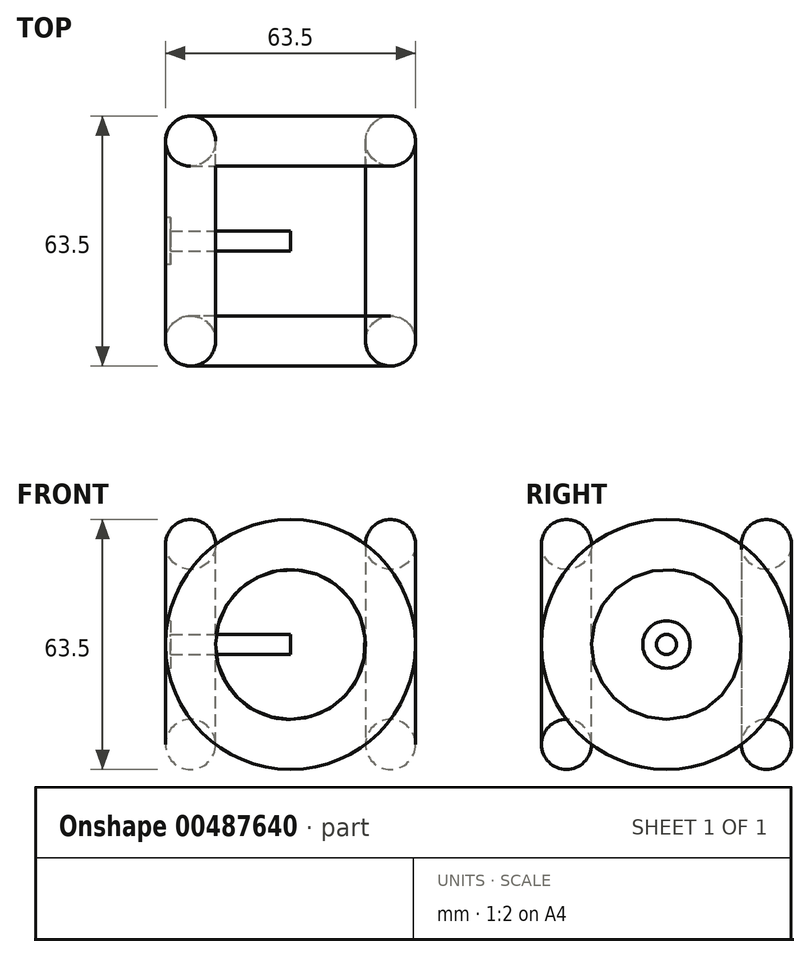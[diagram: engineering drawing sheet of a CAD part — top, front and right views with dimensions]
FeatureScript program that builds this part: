
annotation { "Feature Type Name" : "Feature", "Feature Type Description" : "" }
export const myFeature = defineFeature(function(context is Context, id is Id, definition is map)
    precondition{}
    {
        {
            var Q0;
            Q0=qCreatedBy(makeId("Front.planeOp"),FACE);
            var sketch = newSketch(context, id + "F0", { "sketchPlane" : qUnion([Q0])});
            skLineSegment(sketch, "E0", {"start": v(25.4, 0) * mm, "end": v(25.4, 25.4) * mm});
            skLineSegment(sketch, "E1", {"start": v(25.4, 25.4) * mm, "end": v(-25.4, 25.4) * mm, "construction": true});
            skLineSegment(sketch, "E2", {"start": v(-25.4, 25.4) * mm, "end": v(-25.4, -25.4) * mm, "construction": true});
            skLineSegment(sketch, "E3", {"start": v(-25.4, -25.4) * mm, "end": v(25.4, -25.4) * mm, "construction": true});
            skLineSegment(sketch, "E4", {"start": v(25.4, -25.4) * mm, "end": v(25.4, 0) * mm, "construction": true});
            skLineSegment(sketch, "E5", {"start": v(25.4, 25.4) * mm, "end": v(-25.4, 25.4) * mm});
            skLineSegment(sketch, "E6", {"start": v(-25.4, 25.4) * mm, "end": v(-25.4, -25.4) * mm});
            skLineSegment(sketch, "E7", {"start": v(-25.4, -25.4) * mm, "end": v(25.4, -25.4) * mm});
            skLineSegment(sketch, "E8", {"start": v(25.4, -25.4) * mm, "end": v(25.4, 25.4) * mm});
            skCircle(sketch, "E9", {"center": v(25.4, 25.4) * mm, "radius": 6.35 * mm});
            skCircle(sketch, "E10", {"center": v(-25.4, 25.4) * mm, "radius": 6.35 * mm});
            skLineSegment(sketch, "E11", {"start": v(25.4, 0) * mm, "end": v(-25.4, 0) * mm});
            skSolve(sketch);
        }
        {
            var Q0;
            Q0=qCreatedBy(makeId("Right.planeOp"),FACE);
            var sketch = newSketch(context, id + "F1", { "sketchPlane" : qUnion([Q0])});
            skLineSegment(sketch, "E12", {"start": v(0, 0) * mm, "end": v(0, 25.4) * mm});
            skLineSegment(sketch, "E13", {"start": v(0, 25.4) * mm, "end": v(-25.4, 25.4) * mm});
            skLineSegment(sketch, "E14", {"start": v(-25.4, 25.4) * mm, "end": v(-25.4, -25.4) * mm});
            skLineSegment(sketch, "E15", {"start": v(-25.4, -25.4) * mm, "end": v(25.4, -25.4) * mm});
            skLineSegment(sketch, "E16", {"start": v(25.4, -25.4) * mm, "end": v(25.4, 25.4) * mm});
            skLineSegment(sketch, "E17", {"start": v(25.4, 25.4) * mm, "end": v(-25.4, 25.4) * mm});
            skCircle(sketch, "E18", {"center": v(25.4, 25.4) * mm, "radius": 6.35 * mm});
            skCircle(sketch, "E19", {"center": v(-25.4, 25.4) * mm, "radius": 6.35 * mm});
            skLineSegment(sketch, "E20", {"start": v(-25.4, 0) * mm, "end": v(25.4, 0) * mm});
            skCircle(sketch, "E21", {"center": v(25.4, -25.4) * mm, "radius": 6.35 * mm});
            skLineSegment(sketch, "E22", {"start": v(0, 25.4) * mm, "end": v(0, -25.4) * mm});
            skArc(sketch, "E23", {"start": v(25.4, 0) * mm, "mid": v(0, -25.4) * mm, "end": v(-25.4, 0) * mm});
            skCircle(sketch, "E24", {"center": v(0, 0) * mm, "radius": 2.54 * mm});
            skSolve(sketch);
        }
        {
            var Q0;
            {var subQ0=sQuery(id+"F0.wireOp",EDGE,"E8");var subQ1=sQuery(id+"F0.wireOp",EDGE,"E5");var subQ2=makeQuery(id+"F0.imprint","INTERSECT",VERTEX,{"derivedFrom":[subQ1,subQ0]});Q0=makeQuery(id+"F0.imprint","IMPRINT",FACE,{"disambiguationData":[TD([[makeQuery(id+"F0.imprint","IMPRINT",EDGE,{"disambiguationData":[TD([[subQ2,-1.0]])],"derivedFrom":subQ1}),-1.0]])]});}
            var Q1;
            {var subQ0=sQuery(id+"F0.wireOp",EDGE,"E8");var subQ1=sQuery(id+"F0.wireOp",EDGE,"E5");var subQ2=makeQuery(id+"F0.imprint","INTERSECT",VERTEX,{"derivedFrom":[subQ1,subQ0]});Q1=makeQuery(id+"F0.imprint","IMPRINT",FACE,{"disambiguationData":[TD([[makeQuery(id+"F0.imprint","IMPRINT",EDGE,{"disambiguationData":[TD([[subQ2,-1.0]])],"derivedFrom":subQ1}),1.0]])]});}
            var Q2;
            {var subQ0=sQuery(id+"F0.wireOp",EDGE,"E6");var subQ1=sQuery(id+"F0.wireOp",EDGE,"E5");var subQ2=makeQuery(id+"F0.imprint","INTERSECT",VERTEX,{"derivedFrom":[subQ1,subQ0]});Q2=makeQuery(id+"F0.imprint","IMPRINT",FACE,{"disambiguationData":[TD([[makeQuery(id+"F0.imprint","IMPRINT",EDGE,{"disambiguationData":[TD([[subQ2,1.0]])],"derivedFrom":subQ1}),-1.0]])]});}
            var Q3;
            {var subQ0=sQuery(id+"F0.wireOp",EDGE,"E6");var subQ1=sQuery(id+"F0.wireOp",EDGE,"E5");var subQ2=makeQuery(id+"F0.imprint","INTERSECT",VERTEX,{"derivedFrom":[subQ1,subQ0]});Q3=makeQuery(id+"F0.imprint","IMPRINT",FACE,{"disambiguationData":[TD([[makeQuery(id+"F0.imprint","IMPRINT",EDGE,{"disambiguationData":[TD([[subQ2,1.0]])],"derivedFrom":subQ1}),1.0]])]});}
            var Q4;
            Q4=sQuery(id+"F0.wireOp",EDGE,"E11");
            revolve(context, id + "F2", {"entities" : qUnion([Q0, Q1, Q2, Q3]), "axis" : qUnion([Q4]), "revolveType" : RevolveType.FULL});
        }
        {
            var Q0;
            {var subQ0=sQuery(id+"F1.wireOp",EDGE,"E17");var subQ1=sQuery(id+"F1.wireOp",EDGE,"E16");var subQ2=makeQuery(id+"F1.imprint","INTERSECT",VERTEX,{"derivedFrom":[subQ1,subQ0]});Q0=makeQuery(id+"F1.imprint","IMPRINT",FACE,{"disambiguationData":[TD([[makeQuery(id+"F1.imprint","IMPRINT",EDGE,{"disambiguationData":[TD([[subQ2,1.0]])],"derivedFrom":subQ1}),-1.0]])]});}
            var Q1;
            {var subQ0=sQuery(id+"F1.wireOp",EDGE,"E17");var subQ1=sQuery(id+"F1.wireOp",EDGE,"E16");var subQ2=makeQuery(id+"F1.imprint","INTERSECT",VERTEX,{"derivedFrom":[subQ1,subQ0]});Q1=makeQuery(id+"F1.imprint","IMPRINT",FACE,{"disambiguationData":[TD([[makeQuery(id+"F1.imprint","IMPRINT",EDGE,{"disambiguationData":[TD([[subQ2,1.0]])],"derivedFrom":subQ1}),1.0]])]});}
            var Q2;
            {var subQ0=sQuery(id+"F1.wireOp",EDGE,"E17");var subQ1=sQuery(id+"F1.wireOp",EDGE,"E14");var subQ2=makeQuery(id+"F1.imprint","INTERSECT",VERTEX,{"derivedFrom":[subQ1,subQ0]});Q2=makeQuery(id+"F1.imprint","IMPRINT",FACE,{"disambiguationData":[TD([[makeQuery(id+"F1.imprint","IMPRINT",EDGE,{"disambiguationData":[TD([[subQ2,-1.0]])],"derivedFrom":subQ1}),-1.0]])]});}
            var Q3;
            {var subQ0=sQuery(id+"F1.wireOp",EDGE,"E17");var subQ1=sQuery(id+"F1.wireOp",EDGE,"E14");var subQ2=makeQuery(id+"F1.imprint","INTERSECT",VERTEX,{"derivedFrom":[subQ1,subQ0]});Q3=makeQuery(id+"F1.imprint","IMPRINT",FACE,{"disambiguationData":[TD([[makeQuery(id+"F1.imprint","IMPRINT",EDGE,{"disambiguationData":[TD([[subQ2,-1.0]])],"derivedFrom":subQ1}),1.0]])]});}
            var Q4;
            Q4=sQuery(id+"F1.wireOp",EDGE,"E20");
            revolve(context, id + "F3", {"entities" : qUnion([Q0, Q1, Q2, Q3]), "axis" : qUnion([Q4]), "revolveType" : RevolveType.FULL});
        }
        {
            var Q0;
            Q0=sQuery(id+"F1.wireOp",EDGE,"E18");
            var Q1;
            Q1=sQuery(id+"F1.wireOp",EDGE,"E21");
            var Q2;
            Q2=sQuery(id+"F1.wireOp",EDGE,"E22");
            revolve(context, id + "F4", {"bodyType" : ToolBodyType.SURFACE, "surfaceEntities" : qUnion([Q0, Q1]), "axis" : qUnion([Q2]), "revolveType" : RevolveType.FULL});
        }
        {
            var Q0;
            Q0=sQuery(id+"F1.wireOp",EDGE,"E23");
            var Q1;
            Q1=sQuery(id+"F1.wireOp",EDGE,"E20");
            revolve(context, id + "F5", {"bodyType" : ToolBodyType.SURFACE, "surfaceEntities" : qUnion([Q0]), "axis" : qUnion([Q1]), "revolveType" : RevolveType.FULL});
        }
        {
            var Q0;
            {var subQ0=sQuery(id+"F1.wireOp",EDGE,"E22");var subQ1=sQuery(id+"F1.wireOp",EDGE,"E20");var subQ2=makeQuery(id+"F1.imprint","INTERSECT",VERTEX,{"derivedFrom":[subQ1,subQ0]});Q0=makeQuery(id+"F1.imprint","IMPRINT",FACE,{"disambiguationData":[TD([[makeQuery(id+"F1.imprint","IMPRINT",EDGE,{"disambiguationData":[TD([[subQ2,-1.0]])],"derivedFrom":subQ1}),1.0]])]});}
            var Q1;
            {var subQ0=sQuery(id+"F1.wireOp",EDGE,"E22");var subQ1=sQuery(id+"F1.wireOp",EDGE,"E20");var subQ2=makeQuery(id+"F1.imprint","INTERSECT",VERTEX,{"derivedFrom":[subQ1,subQ0]});Q1=makeQuery(id+"F1.imprint","IMPRINT",FACE,{"disambiguationData":[TD([[makeQuery(id+"F1.imprint","IMPRINT",EDGE,{"disambiguationData":[TD([[subQ2,-1.0]])],"derivedFrom":subQ1}),-1.0]])]});}
            var Q2;
            {var subQ0=sQuery(id+"F1.wireOp",EDGE,"E24");var subQ1=sQuery(id+"F1.wireOp",EDGE,"E20");var subQ2=makeQuery(id+"F1.imprint","INTERSECT",VERTEX,{"disambiguationData":[OD(0.0)],"derivedFrom":[subQ1,subQ0]});Q2=makeQuery(id+"F1.imprint","IMPRINT",FACE,{"disambiguationData":[TD([[makeQuery(id+"F1.imprint","IMPRINT",EDGE,{"disambiguationData":[TD([[subQ2,-1.0]])],"derivedFrom":subQ1}),-1.0]])]});}
            var Q3;
            {var subQ0=sQuery(id+"F1.wireOp",EDGE,"E24");var subQ1=sQuery(id+"F1.wireOp",EDGE,"E20");var subQ2=makeQuery(id+"F1.imprint","INTERSECT",VERTEX,{"disambiguationData":[OD(0.0)],"derivedFrom":[subQ1,subQ0]});Q3=makeQuery(id+"F1.imprint","IMPRINT",FACE,{"disambiguationData":[TD([[makeQuery(id+"F1.imprint","IMPRINT",EDGE,{"disambiguationData":[TD([[subQ2,-1.0]])],"derivedFrom":subQ1}),1.0]])]});}
            extrude(context, id + "F6", {"entities" : qUnion([Q0, Q1, Q2, Q3]), "oppositeDirection" : true, "depth" : 31.75 * mm});
        }
        {
            var Q0;
            Q0=makeQuery(id+"F6.opExtrude","CAP_FACE",FACE,{"disambiguationData":[OSD([sQuery(id+"F1.wireOp",EDGE,"E24")])],"isStart":false});
            var sketch = newSketch(context, id + "F7", { "sketchPlane" : qUnion([Q0])});
            skCircle(sketch, "E25", {"center": v(0, 0) * mm, "radius": 6.03 * mm});
            skSolve(sketch);
        }
        {
            var Q0;
            Q0=makeQuery(id+"F7.imprint","IMPRINT",FACE,{"disambiguationData":[TD([[makeQuery(id+"F7.imprint","IMPRINT",EDGE,{"derivedFrom":sQuery(id+"F7.wireOp",EDGE,"E25")}),1.0]])]});
            extrude(context, id + "F8", {"entities" : qUnion([Q0]), "operationType" : NewBodyOperationType.ADD, "oppositeDirection" : true, "depth" : 1.27 * mm});
        }
    });
